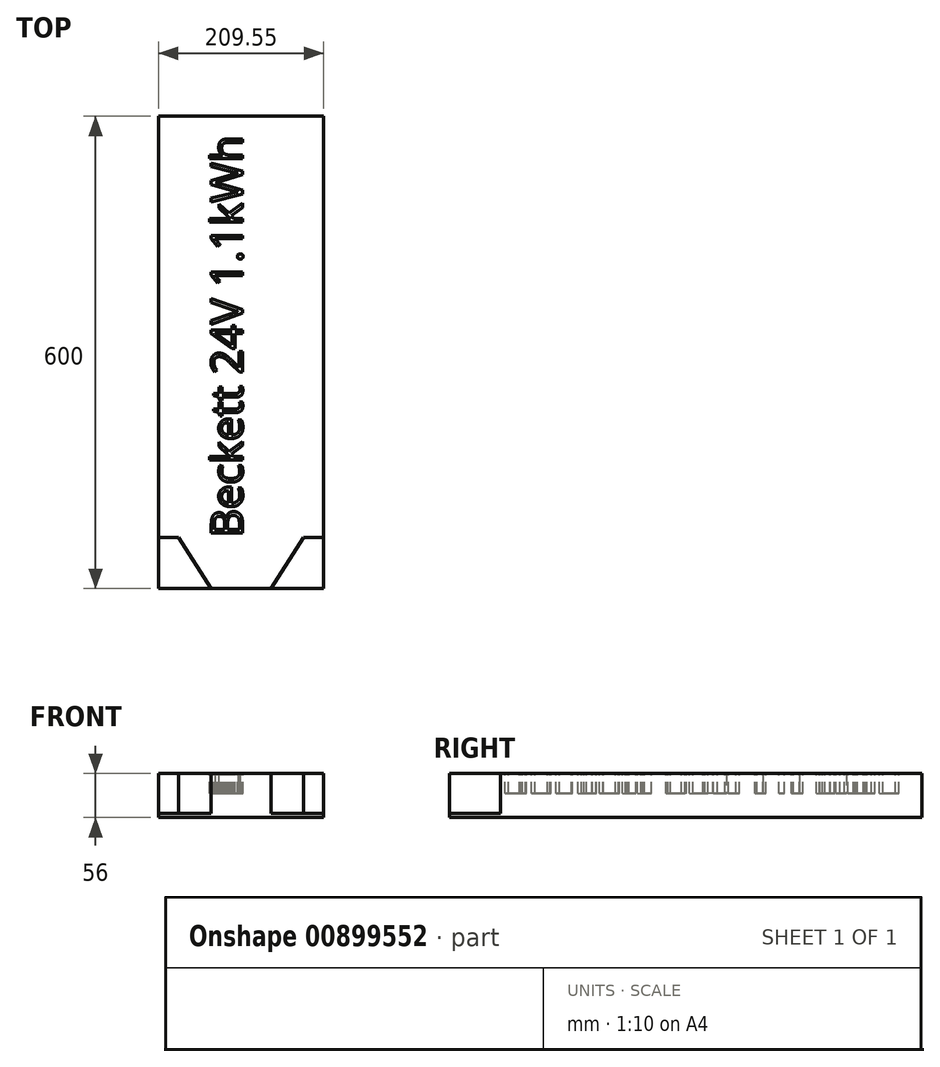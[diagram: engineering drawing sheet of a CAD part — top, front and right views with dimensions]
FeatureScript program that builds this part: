
annotation { "Feature Type Name" : "Feature", "Feature Type Description" : "" }
export const myFeature = defineFeature(function(context is Context, id is Id, definition is map)
    precondition{}
    {
        {
            var Q0;
            Q0=qCreatedBy(makeId("Top.planeOp"),FACE);
            var sketch = newSketch(context, id + "F0", { "sketchPlane" : qUnion([Q0])});
            skLineSegment(sketch, "E0.bottom", {"start": v(0, 0) * mm, "end": v(209.55, 0) * mm});
            skLineSegment(sketch, "E0.top", {"start": v(0, 600) * mm, "end": v(209.55, 600) * mm});
            skLineSegment(sketch, "E0.left", {"start": v(0, 0) * mm, "end": v(0, 600) * mm});
            skLineSegment(sketch, "E0.right", {"start": v(209.55, 0) * mm, "end": v(209.55, 600) * mm});
            skSolve(sketch);
        }
        {
            var Q0;
            Q0=makeQuery(id+"F0.imprint","IMPRINT",FACE,{"disambiguationData":[TD([[makeQuery(id+"F0.imprint","IMPRINT",EDGE,{"derivedFrom":sQuery(id+"F0.wireOp",EDGE,"E0.bottom")}),1.0]])]});
            extrude(context, id + "F1", {"entities" : qUnion([Q0]), "depth" : 56 * mm, "offsetDistance" : 25.4 * mm});
        }
        {
            var Q0;
            Q0=makeQuery(id+"F1.opExtrude","CAP_FACE",FACE,{"disambiguationData":[OSD([sQuery(id+"F0.wireOp",EDGE,"E0.bottom"),sQuery(id+"F0.wireOp",EDGE,"E0.top"),sQuery(id+"F0.wireOp",EDGE,"E0.left"),sQuery(id+"F0.wireOp",EDGE,"E0.right")])],"isStart":false});
            var sketch = newSketch(context, id + "F2", { "sketchPlane" : qUnion([Q0])});
            skLineSegment(sketch, "E1.bottom", {"start": v(209.55, 0) * mm, "end": v(142.88, 0) * mm});
            skLineSegment(sketch, "E1.top", {"start": v(209.55, 64.94) * mm, "end": v(184.15, 64.94) * mm});
            skLineSegment(sketch, "E1.left", {"start": v(209.55, 0) * mm, "end": v(209.55, 64.94) * mm});
            skLineSegment(sketch, "E1.right", {"start": v(0, 0) * mm, "end": v(0, 64.94) * mm});
            skLineSegment(sketch, "E2", {"start": v(104.78, 0) * mm, "end": v(104.78, 64.94) * mm, "construction": true});
            skLineSegment(sketch, "E3", {"start": v(25.4, 64.94) * mm, "end": v(66.68, 0) * mm});
            skLineSegment(sketch, "E4.MirrorCS", {"start": v(184.15, 64.94) * mm, "end": v(142.88, 0) * mm});
            skLineSegment(sketch, "E5.trimOffspring", {"start": v(25.4, 64.94) * mm, "end": v(0, 64.94) * mm});
            skLineSegment(sketch, "E6.trimOffspring", {"start": v(66.68, 0) * mm, "end": v(0, 0) * mm});
            skSolve(sketch);
        }
        {
            var Q0;
            Q0 = qSketchRegion(id + "F2", true);
            extrude(context, id + "F3", {"entities" : qUnion([Q0]), "operationType" : NewBodyOperationType.REMOVE, "oppositeDirection" : true, "depth" : 50.8 * mm, "offsetDistance" : 25.4 * mm});
        }
        {
            var Q0;
            Q0=makeQuery(id+"F1.opExtrude","CAP_FACE",FACE,{"disambiguationData":[OSD([sQuery(id+"F0.wireOp",EDGE,"E0.bottom"),sQuery(id+"F0.wireOp",EDGE,"E0.top"),sQuery(id+"F0.wireOp",EDGE,"E0.left"),sQuery(id+"F0.wireOp",EDGE,"E0.right")])],"isStart":false});
            var sketch = newSketch(context, id + "F4", { "sketchPlane" : qUnion([Q0])});
            skText(sketch, "E7", { "text": "Beckett 24V 1.1kWh", "fontName": "OpenSans-Regular.ttf"});
            const initialGuessF4  = {"E7": [0.1066, 0.06494, 0, 1, 0.03992]};
            skSetInitialGuess(sketch, initialGuessF4);
            skSolve(sketch);
        }
        {
            var Q0;
            Q0 = qSketchRegion(id + "F4", true);
            extrude(context, id + "F5", {"entities" : qUnion([Q0]), "operationType" : NewBodyOperationType.REMOVE, "oppositeDirection" : true, "depth" : 25.4 * mm, "offsetDistance" : 25.4 * mm});
        }
    });
